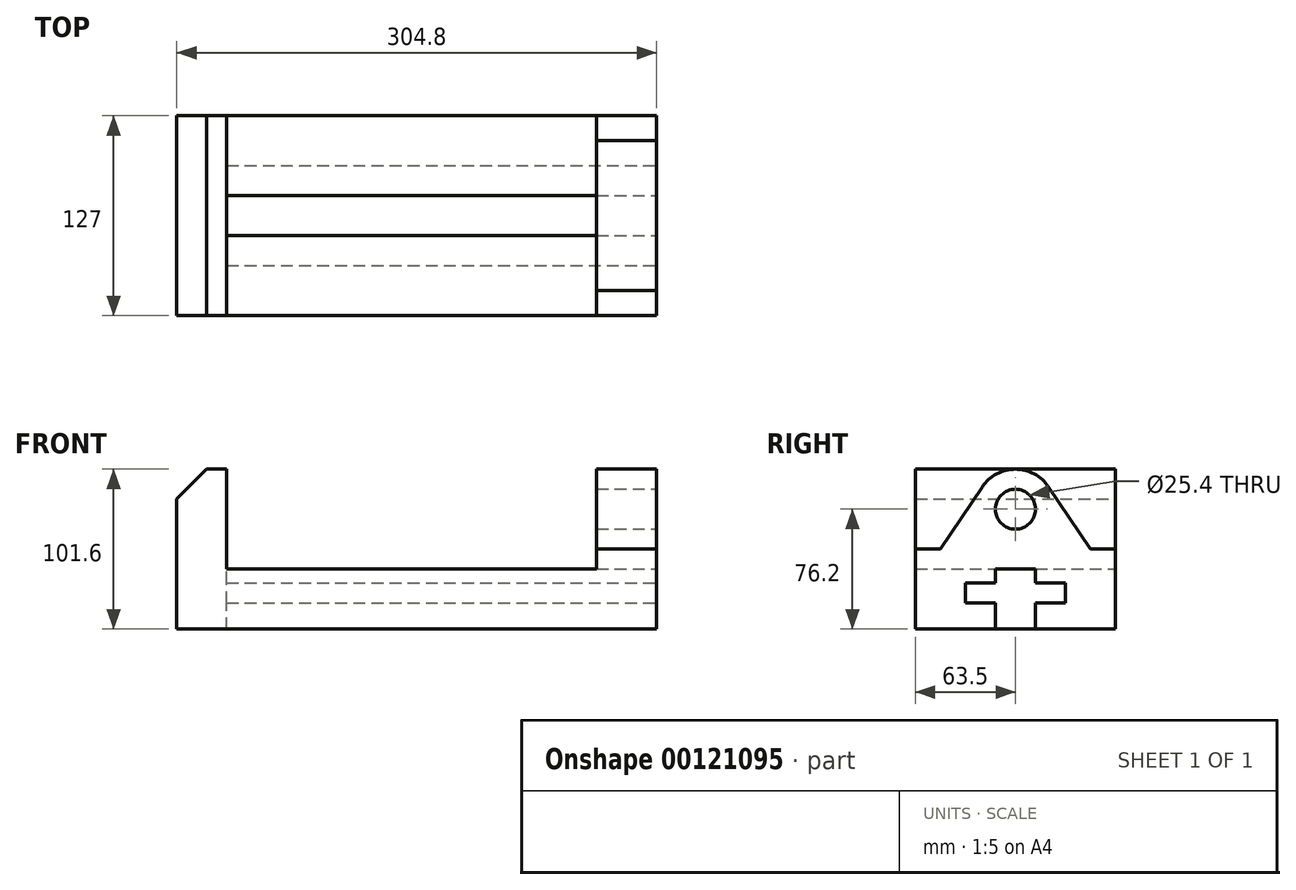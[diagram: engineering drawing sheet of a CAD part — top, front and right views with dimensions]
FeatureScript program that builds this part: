
annotation { "Feature Type Name" : "Feature", "Feature Type Description" : "" }
export const myFeature = defineFeature(function(context is Context, id is Id, definition is map)
    precondition{}
    {
        {
            var Q0;
            Q0=qCreatedBy(makeId("Front.planeOp"),FACE);
            var sketch = newSketch(context, id + "F0", { "sketchPlane" : qUnion([Q0])});
            skLineSegment(sketch, "E0", {"start": v(0, 0) * mm, "end": v(0, 82.55) * mm});
            skLineSegment(sketch, "E1", {"start": v(0, 82.55) * mm, "end": v(19.05, 101.6) * mm});
            skLineSegment(sketch, "E2", {"start": v(19.05, 101.6) * mm, "end": v(31.75, 101.6) * mm});
            skLineSegment(sketch, "E3", {"start": v(31.75, 101.6) * mm, "end": v(31.75, 38.1) * mm});
            skLineSegment(sketch, "E4", {"start": v(31.75, 38.1) * mm, "end": v(266.7, 38.1) * mm});
            skLineSegment(sketch, "E5", {"start": v(266.7, 38.1) * mm, "end": v(266.7, 101.6) * mm});
            skLineSegment(sketch, "E6", {"start": v(266.7, 101.6) * mm, "end": v(304.8, 101.6) * mm});
            skLineSegment(sketch, "E7", {"start": v(304.8, 101.6) * mm, "end": v(304.8, 0) * mm});
            skLineSegment(sketch, "E8", {"start": v(304.8, 0) * mm, "end": v(0, 0) * mm});
            skSolve(sketch);
        }
        {
            var Q0;
            Q0 = qSketchRegion(id + "F0", true);
            extrude(context, id + "F1", {"entities" : qUnion([Q0]), "endBound" : BoundingType.SYMMETRIC, "depth" : 127 * mm});
        }
        {
            var Q0;
            Q0=makeQuery(id+"F1.opExtrude","SWEPT_FACE",FACE,{"disambiguationData":[OSD([sQuery(id+"F0.wireOp",EDGE,"E7")])]});
            var sketch = newSketch(context, id + "F2", { "sketchPlane" : qUnion([Q0])});
            skLineSegment(sketch, "E9", {"start": v(-12.7, 0) * mm, "end": v(-12.7, 16.51) * mm});
            skLineSegment(sketch, "E10", {"start": v(-12.7, 16.51) * mm, "end": v(-31.75, 16.51) * mm});
            skLineSegment(sketch, "E11", {"start": v(-31.75, 16.5) * mm, "end": v(-31.75, 29.2) * mm});
            skLineSegment(sketch, "E12", {"start": v(-31.75, 29.2) * mm, "end": v(-12.7, 29.2) * mm});
            skLineSegment(sketch, "E13", {"start": v(-12.7, 29.2) * mm, "end": v(-12.7, 38.1) * mm});
            skLineSegment(sketch, "E14", {"start": v(-12.7, 38.1) * mm, "end": v(12.7, 38.1) * mm});
            skLineSegment(sketch, "E15", {"start": v(12.7, 38.1) * mm, "end": v(12.7, 29.2) * mm});
            skLineSegment(sketch, "E16", {"start": v(12.7, 29.2) * mm, "end": v(31.75, 29.21) * mm});
            skLineSegment(sketch, "E17", {"start": v(31.75, 29.21) * mm, "end": v(31.75, 16.51) * mm});
            skLineSegment(sketch, "E18", {"start": v(31.75, 16.51) * mm, "end": v(12.7, 16.51) * mm});
            skLineSegment(sketch, "E19", {"start": v(12.7, 16.51) * mm, "end": v(12.7, 0) * mm});
            skLineSegment(sketch, "E20", {"start": v(12.7, 0) * mm, "end": v(-12.7, 0) * mm});
            skSolve(sketch);
        }
        {
            var Q0;
            Q0 = qSketchRegion(id + "F2", true);
            extrude(context, id + "F3", {"entities" : qUnion([Q0]), "operationType" : NewBodyOperationType.REMOVE, "oppositeDirection" : true, "depth" : 273.05 * mm});
        }
        {
            var Q0;
            Q0=makeQuery(id+"F1.opExtrude","SWEPT_FACE",FACE,{"disambiguationData":[OSD([sQuery(id+"F0.wireOp",EDGE,"E7")])]});
            var sketch = newSketch(context, id + "F4", { "sketchPlane" : qUnion([Q0])});
            skLineSegment(sketch, "E21", {"start": v(-63.5, 50.8) * mm, "end": v(-47.62, 50.8) * mm});
            skLineSegment(sketch, "E22", {"start": v(47.63, 50.8) * mm, "end": v(63.5, 50.8) * mm});
            skArc(sketch, "E23", {"start": v(-21.1, 90.35) * mm, "mid": v(0, 101.6) * mm, "end": v(21.1, 90.35) * mm});
            skPoint(sketch, "E23.centerSnap0", {"position": v(0, 101.6) * mm});
            skLineSegment(sketch, "E24", {"start": v(-47.62, 50.8) * mm, "end": v(-21.1, 90.35) * mm});
            skLineSegment(sketch, "E25", {"start": v(47.62, 50.8) * mm, "end": v(21.1, 90.35) * mm});
            skLineSegment(sketch, "E26", {"start": v(-63.5, 50.8) * mm, "end": v(-63.5, 101.6) * mm});
            skLineSegment(sketch, "E27", {"start": v(-63.5, 101.6) * mm, "end": v(0, 101.6) * mm});
            skLineSegment(sketch, "E28", {"start": v(63.5, 101.6) * mm, "end": v(63.5, 50.8) * mm});
            skCircle(sketch, "E29", {"center": v(0, 76.2) * mm, "radius": 12.7 * mm});
            skSolve(sketch);
        }
        {
            var Q0;
            Q0 = qSketchRegion(id + "F4", true);
            var Q1;
            Q1=makeQuery(id+"F4.imprint","IMPRINT",FACE,{"disambiguationData":[TD([[makeQuery(id+"F4.imprint","IMPRINT",EDGE,{"derivedFrom":sQuery(id+"F4.wireOp",EDGE,"E22")}),1.0]])]});
            extrude(context, id + "F5", {"entities" : qUnion([Q0, Q1]), "operationType" : NewBodyOperationType.REMOVE, "oppositeDirection" : true, "depth" : 38.1 * mm});
        }
    });
